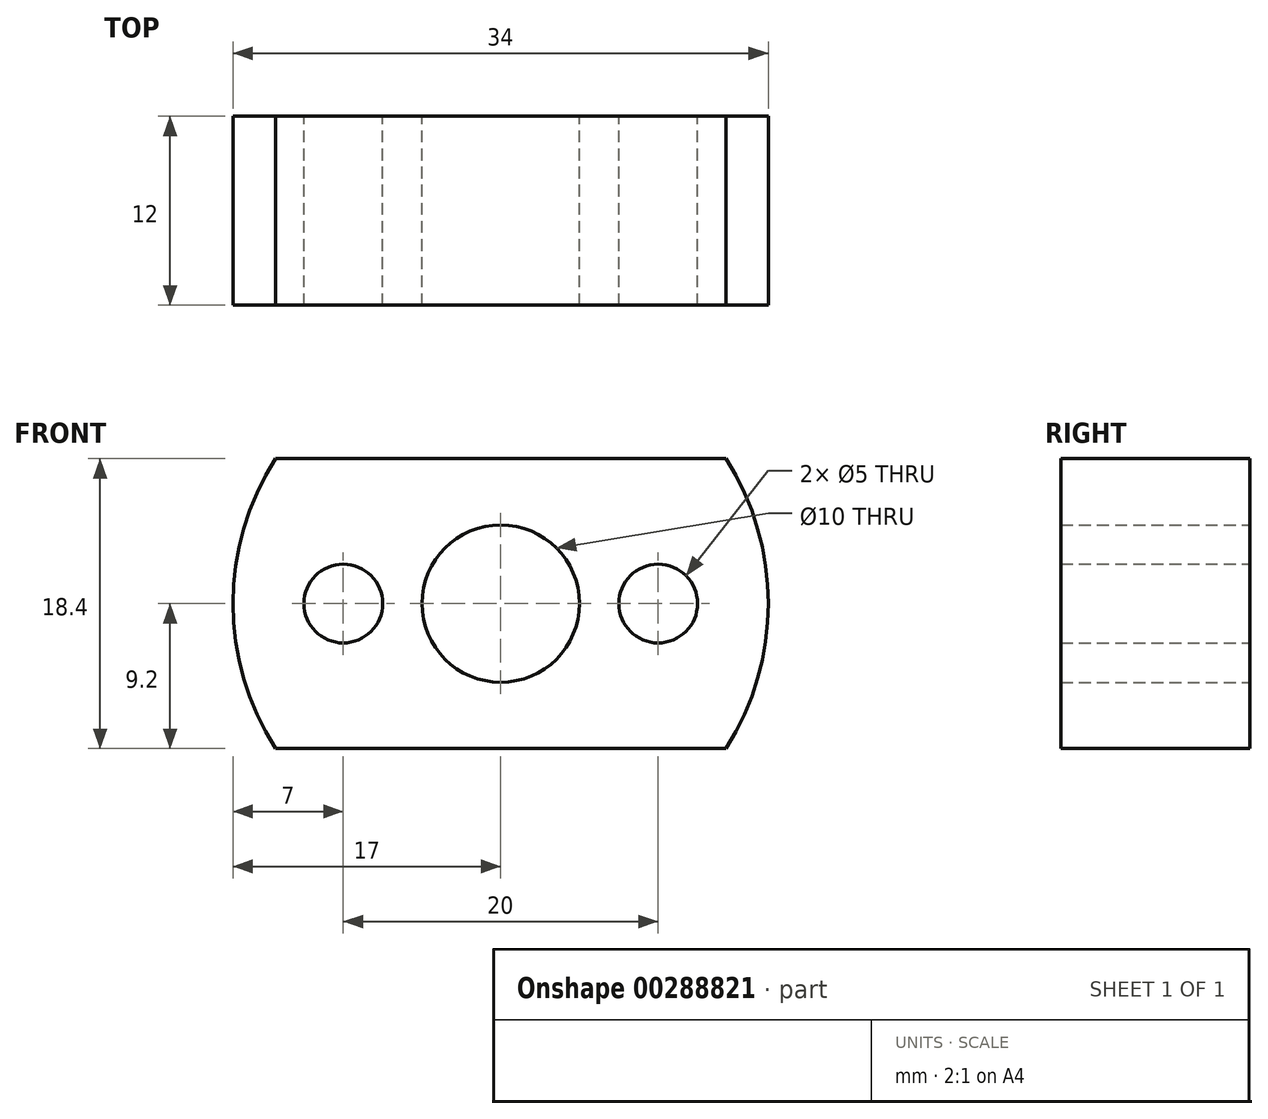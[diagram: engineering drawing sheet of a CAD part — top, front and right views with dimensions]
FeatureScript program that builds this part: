
annotation { "Feature Type Name" : "Feature", "Feature Type Description" : "" }
export const myFeature = defineFeature(function(context is Context, id is Id, definition is map)
    precondition{}
    {
        {
            var Q0;
            Q0=qCreatedBy(makeId("Front.planeOp"),FACE);
            var sketch = newSketch(context, id + "F0", { "sketchPlane" : qUnion([Q0])});
            skCircle(sketch, "E0", {"center": v(0, 0) * mm, "radius": 17 * mm});
            skCircle(sketch, "E1", {"center": v(-10, 0) * mm, "radius": 2.5 * mm});
            skCircle(sketch, "E2", {"center": v(10, 0) * mm, "radius": 2.5 * mm});
            skCircle(sketch, "E3", {"center": v(0, 0) * mm, "radius": 5 * mm});
            skSolve(sketch);
        }
        {
            var Q0;
            Q0=makeQuery(id+"F0.imprint","IMPRINT",FACE,{"disambiguationData":[TD([[makeQuery(id+"F0.imprint","IMPRINT",EDGE,{"derivedFrom":sQuery(id+"F0.wireOp",EDGE,"E0")}),1.0]])]});
            extrude(context, id + "F1", {"entities" : qUnion([Q0]), "depth" : 12 * mm});
        }
        {
            var Q0;
            Q0=makeQuery(id+"F1.opExtrude","CAP_FACE",FACE,{"disambiguationData":[OSD([sQuery(id+"F0.wireOp",EDGE,"E0"),sQuery(id+"F0.wireOp",EDGE,"E1"),sQuery(id+"F0.wireOp",EDGE,"E2"),sQuery(id+"F0.wireOp",EDGE,"E3")])],"isStart":true});
            var sketch = newSketch(context, id + "F2", { "sketchPlane" : qUnion([Q0])});
            skLineSegment(sketch, "E4.bottom", {"start": v(-24.02, 9.2) * mm, "end": v(24.02, 9.2) * mm});
            skLineSegment(sketch, "E4.top", {"start": v(-24.02, -9.2) * mm, "end": v(24.02, -9.2) * mm});
            skLineSegment(sketch, "E4.left", {"start": v(-24.02, 9.2) * mm, "end": v(-24.02, -9.2) * mm});
            skLineSegment(sketch, "E4.right", {"start": v(24.02, 9.2) * mm, "end": v(24.02, -9.2) * mm});
            skLineSegment(sketch, "E5", {"start": v(-24.02, 0) * mm, "end": v(24.02, 0) * mm, "construction": true});
            skSolve(sketch);
        }
        {
            var Q0;
            {var subQ0=sQuery(id+"F2.wireOp",EDGE,"E4.bottom");var subQ1=makeQuery(id+"F1.opExtrude","CAP_EDGE",EDGE,{"disambiguationData":[OSD([sQuery(id+"F0.wireOp",EDGE,"E0")])],"isStart":true});var subQ2=makeQuery(id+"F2.imprint","INTERSECT",VERTEX,{"disambiguationData":[OD(0.0)],"derivedFrom":[subQ1,subQ0]});Q0=makeQuery(id+"F2.imprint","IMPRINT",FACE,{"disambiguationData":[TD([[makeQuery(id+"F2.imprint","IMPRINT",EDGE,{"disambiguationData":[TD([[subQ2,-1.0]])],"derivedFrom":subQ0}),1.0]])]});}
            var Q1;
            {var subQ0=sQuery(id+"F2.wireOp",EDGE,"E4.top");var subQ1=makeQuery(id+"F1.opExtrude","CAP_EDGE",EDGE,{"disambiguationData":[OSD([sQuery(id+"F0.wireOp",EDGE,"E0")])],"isStart":true});var subQ2=makeQuery(id+"F2.imprint","INTERSECT",VERTEX,{"disambiguationData":[OD(0.0)],"derivedFrom":[subQ1,subQ0]});Q1=makeQuery(id+"F2.imprint","IMPRINT",FACE,{"disambiguationData":[TD([[makeQuery(id+"F2.imprint","IMPRINT",EDGE,{"disambiguationData":[TD([[subQ2,-1.0]])],"derivedFrom":subQ0}),-1.0]])]});}
            extrude(context, id + "F3", {"entities" : qUnion([Q0, Q1]), "operationType" : NewBodyOperationType.REMOVE, "oppositeDirection" : true, "depth" : 25 * mm});
        }
    });
